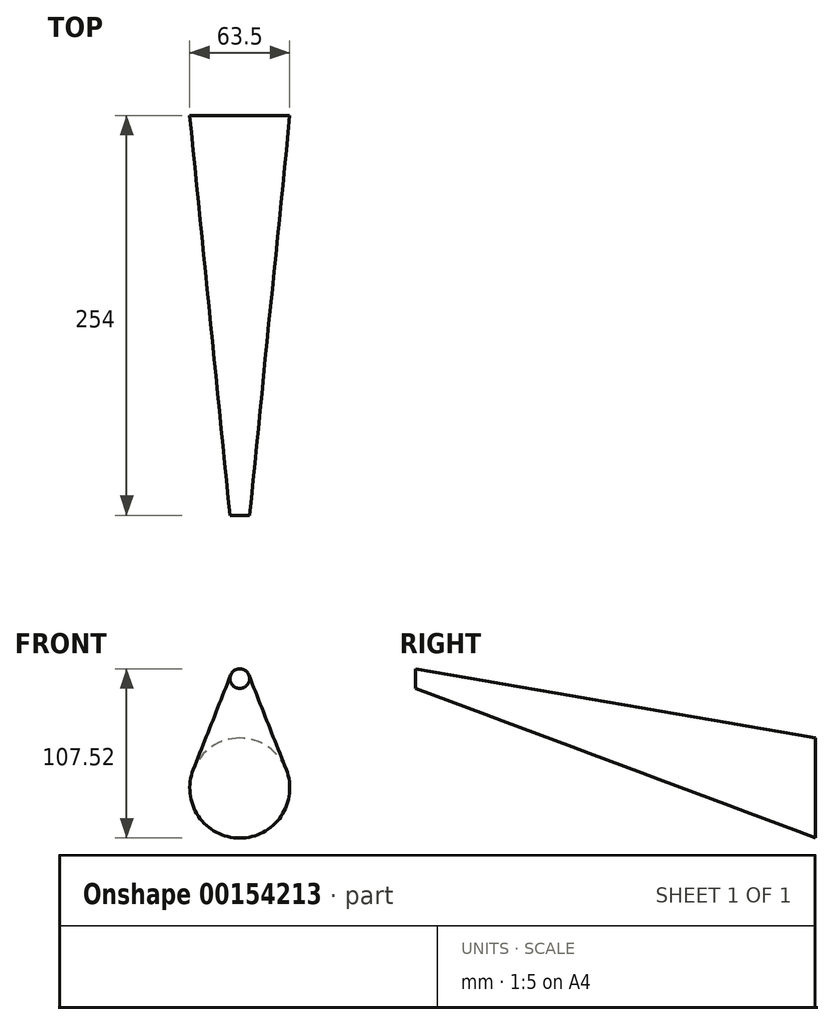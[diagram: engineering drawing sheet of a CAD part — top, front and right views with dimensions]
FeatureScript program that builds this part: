
annotation { "Feature Type Name" : "Feature", "Feature Type Description" : "" }
export const myFeature = defineFeature(function(context is Context, id is Id, definition is map)
    precondition{}
    {
        {
            var Q0;
            Q0=qCreatedBy(makeId("Front.planeOp"),FACE);
            var sketch = newSketch(context, id + "F0", { "sketchPlane" : qUnion([Q0])});
            skArc(sketch, "E0", {"start": v(0, -31.75) * mm, "mid": v(31.75, 0) * mm, "end": v(0, 31.75) * mm});
            skCircle(sketch, "E1", {"center": v(0, 0) * mm, "radius": 31.75 * mm});
            skSolve(sketch);
        }
        {
            var Q0;
            Q0=makeQuery(id+"F0.imprint","IMPRINT",FACE,{"disambiguationData":[TD([[makeQuery(id+"F0.imprint","IMPRINT",EDGE,{"derivedFrom":sQuery(id+"F0.wireOp",EDGE,"E1")}),1.0]])]});
            cPlane(context, id + "F1", {"entities" : qUnion([Q0]), "cplaneType" : CPlaneType.OFFSET, "offset" : 254 * mm, "width" : 152.4 * mm, "height" : 152.4 * mm});
        }
        {
            var Q0;
            Q0=qCreatedBy(id+"F1.planeOp",FACE);
            var sketch = newSketch(context, id + "F2", { "sketchPlane" : qUnion([Q0])});
            skCircle(sketch, "E2", {"center": v(0, 69.55) * mm, "radius": 6.21 * mm});
            skSolve(sketch);
        }
        {
            var Q0;
            Q0=makeQuery(id+"F0.imprint","IMPRINT",FACE,{"disambiguationData":[TD([[makeQuery(id+"F0.imprint","IMPRINT",EDGE,{"derivedFrom":sQuery(id+"F0.wireOp",EDGE,"E1")}),1.0]])]});
            var Q1;
            Q1=makeQuery(id+"F2.imprint","IMPRINT",FACE,{"disambiguationData":[TD([[makeQuery(id+"F2.imprint","IMPRINT",EDGE,{"derivedFrom":sQuery(id+"F2.wireOp",EDGE,"E2")}),1.0]])]});
            loft(context, id + "F3", {"sheetProfilesArray" : [{ "sheetProfileEntities" : qUnion([Q0]) }, { "sheetProfileEntities" : qUnion([Q1]) }]});
        }
    });
